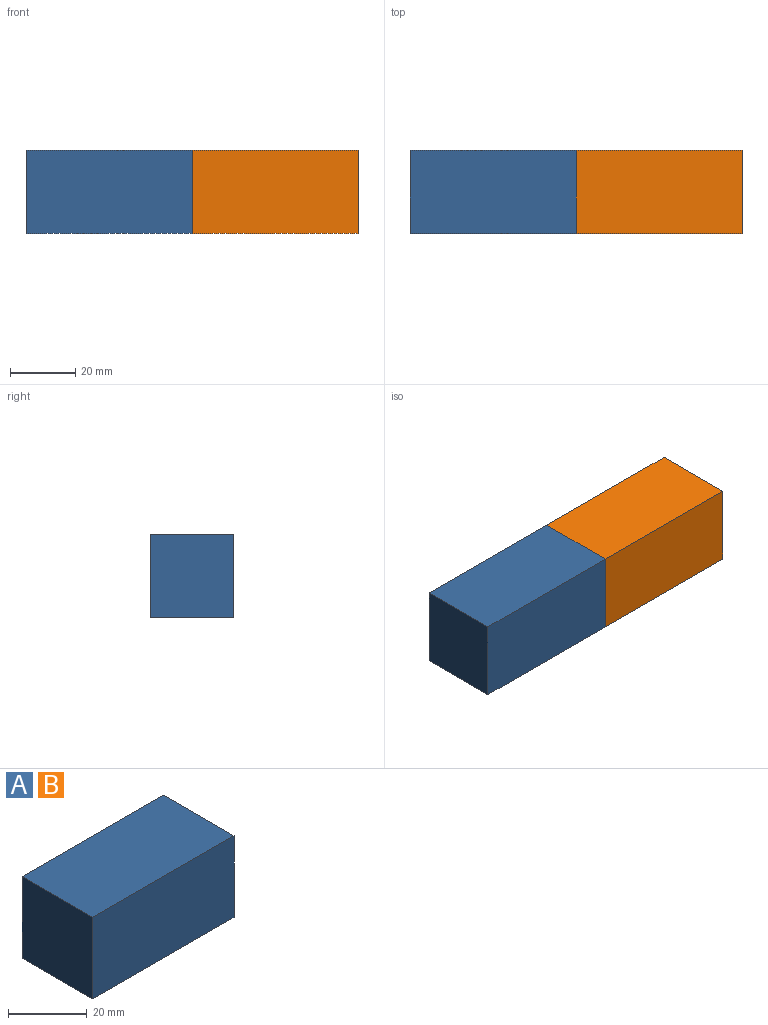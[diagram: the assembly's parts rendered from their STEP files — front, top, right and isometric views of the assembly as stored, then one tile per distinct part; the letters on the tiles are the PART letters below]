
ASSEMBLY  parts=2 mates=1
PART A: 6 faces, bbox 50.8x25.4x25.4 mm
  f0: plane 25.4x25.4mm, normal (-1,0,0), area 645.2mm2, adj f1,f3,f4,f5
  f1: plane 50.8x25.4mm, normal (0,-1,0), area 1290.3mm2, adj f0,f2,f4,f5
  f2: plane 25.4x25.4mm, normal (1,0,0), area 645.2mm2, adj f1,f3,f4,f5
  f3: plane 50.8x25.4mm, normal (0,1,0), area 1290.3mm2, adj f0,f2,f4,f5
  f4: plane 50.8x25.4mm, normal (0,0,1), area 1290.3mm2, adj f0,f1,f2,f3
  f5: plane 50.8x25.4mm, normal (0,0,-1), area 1290.3mm2, adj f0,f1,f2,f3
PART B: same geometry as A
PLACE A at identity
PLACE B t=(50.8,0,0)mm
MATE planar A.f2 <-> B.f0  axis (1,0,0) through (50.8,12.7,12.7)mm
